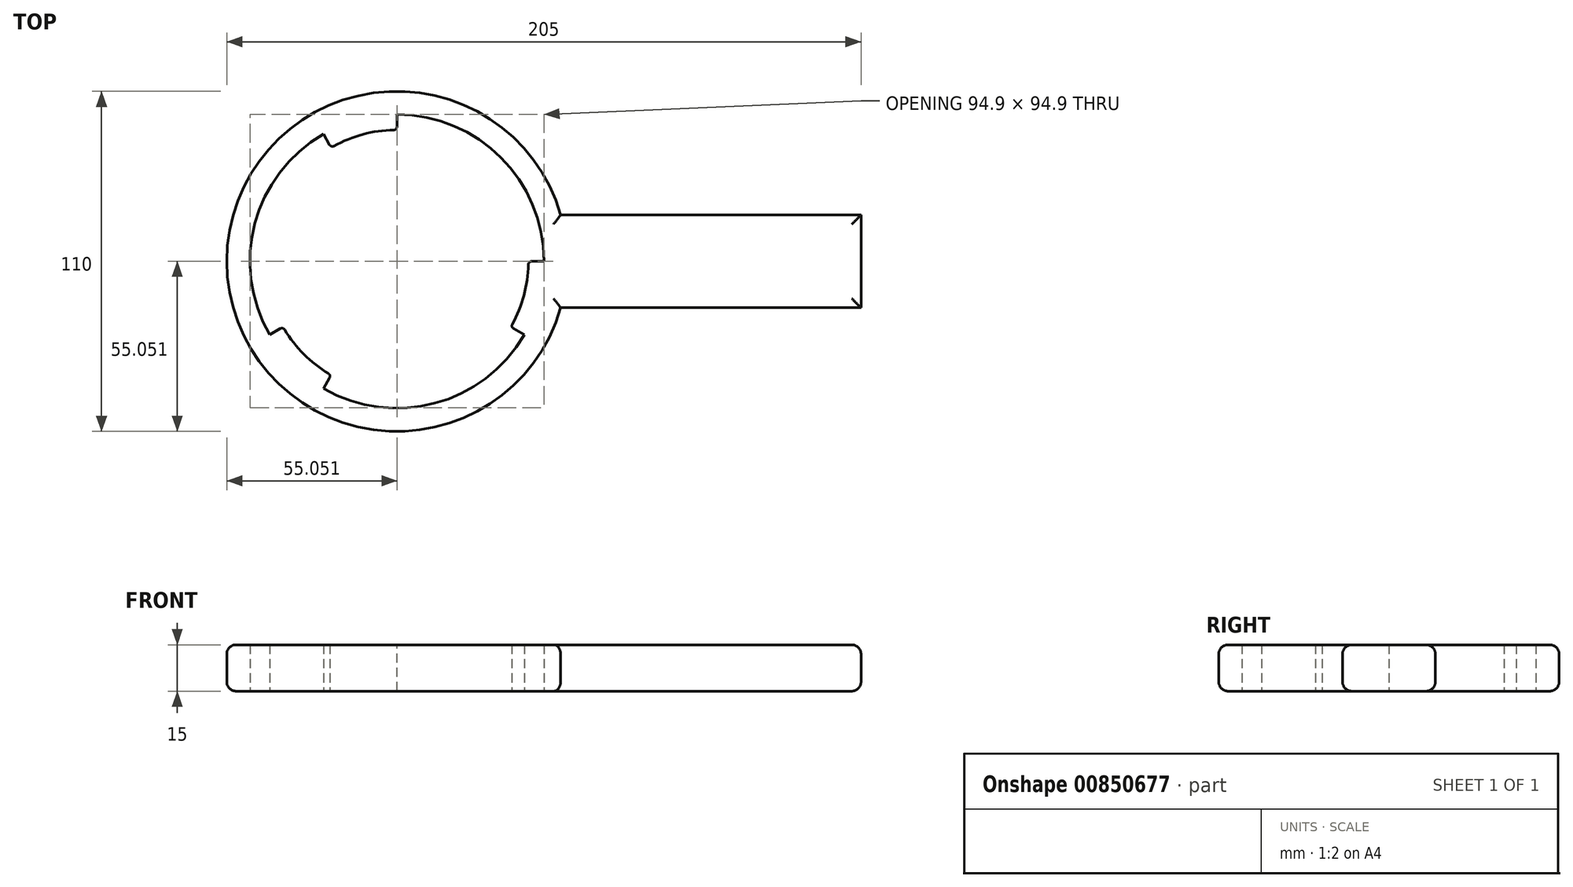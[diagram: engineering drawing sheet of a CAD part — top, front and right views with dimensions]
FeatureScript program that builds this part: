
annotation { "Feature Type Name" : "Feature", "Feature Type Description" : "" }
export const myFeature = defineFeature(function(context is Context, id is Id, definition is map)
    precondition{}
    {
        {
            var Q0;
            Q0=qCreatedBy(makeId("Top.planeOp"),FACE);
            var sketch = newSketch(context, id + "F0", { "sketchPlane" : qUnion([Q0])});
            skArc(sketch, "E0", {"start": v(-36.8, -21.25) * mm, "mid": v(-30.05, -30.05) * mm, "end": v(-21.25, -36.8) * mm});
            skArc(sketch, "E1", {"start": v(-23.75, -41.14) * mm, "mid": v(12.3, -45.88) * mm, "end": v(41.14, -23.75) * mm});
            skArc(sketch, "E2", {"start": v(52.92, 15) * mm, "mid": v(-55, 0) * mm, "end": v(52.92, -15) * mm});
            skLineSegment(sketch, "E3", {"start": v(0, 42.5) * mm, "end": v(0, 47.5) * mm});
            skLineSegment(sketch, "E4", {"start": v(-21.25, 36.8) * mm, "end": v(-23.75, 41.14) * mm});
            skLineSegment(sketch, "E5", {"start": v(-36.8, -21.25) * mm, "end": v(-41.14, -23.75) * mm});
            skLineSegment(sketch, "E6", {"start": v(-21.25, -36.8) * mm, "end": v(-23.75, -41.14) * mm});
            skLineSegment(sketch, "E7", {"start": v(36.8, -21.25) * mm, "end": v(41.14, -23.75) * mm});
            skLineSegment(sketch, "E8", {"start": v(42.5, 0) * mm, "end": v(47.5, 0) * mm});
            skArc(sketch, "E9.trimOffspring", {"start": v(0, 42.5) * mm, "mid": v(-11, 41.05) * mm, "end": v(-21.25, 36.8) * mm});
            skArc(sketch, "E10.trimOffspring", {"start": v(36.8, -21.25) * mm, "mid": v(41.05, -11) * mm, "end": v(42.5, 0) * mm});
            skArc(sketch, "E11.trimOffspring", {"start": v(-23.75, 41.14) * mm, "mid": v(-45.88, 12.3) * mm, "end": v(-41.14, -23.75) * mm});
            skArc(sketch, "E12.trimOffspring", {"start": v(47.5, 0) * mm, "mid": v(33.59, 33.59) * mm, "end": v(0, 47.5) * mm});
            skLineSegment(sketch, "E13", {"start": v(52.92, 15) * mm, "end": v(150, 15) * mm});
            skLineSegment(sketch, "E14", {"start": v(150, 15) * mm, "end": v(150, -15) * mm});
            skLineSegment(sketch, "E15", {"start": v(150, -15) * mm, "end": v(52.92, -15) * mm});
            skSolve(sketch);
        }
        {
            var Q0;
            Q0=makeQuery(id+"F0.imprint","IMPRINT",FACE,{"disambiguationData":[TD([[makeQuery(id+"F0.imprint","IMPRINT",EDGE,{"derivedFrom":sQuery(id+"F0.wireOp",EDGE,"E0")}),-1.0]])]});
            extrude(context, id + "F1", {"entities" : qUnion([Q0]), "depth" : 15 * mm, "offsetDistance" : 25 * mm});
        }
        {
            var Q0;
            Q0=makeQuery(id+"F1.opExtrude","CAP_EDGE",EDGE,{"disambiguationData":[OSD([sQuery(id+"F0.wireOp",EDGE,"E13")])],"isStart":false});
            var Q1;
            Q1=makeQuery(id+"F1.opExtrude","CAP_EDGE",EDGE,{"disambiguationData":[OSD([sQuery(id+"F0.wireOp",EDGE,"E14")])],"isStart":false});
            var Q2;
            Q2=makeQuery(id+"F1.opExtrude","CAP_EDGE",EDGE,{"disambiguationData":[OSD([sQuery(id+"F0.wireOp",EDGE,"E15")])],"isStart":false});
            var Q3;
            Q3=makeQuery(id+"F1.opExtrude","CAP_EDGE",EDGE,{"disambiguationData":[OSD([sQuery(id+"F0.wireOp",EDGE,"E2")])],"isStart":false});
            var Q4;
            Q4=makeQuery(id+"F1.opExtrude","CAP_EDGE",EDGE,{"disambiguationData":[OSD([sQuery(id+"F0.wireOp",EDGE,"E15")])],"isStart":true});
            var Q5;
            Q5=makeQuery(id+"F1.opExtrude","CAP_EDGE",EDGE,{"disambiguationData":[OSD([sQuery(id+"F0.wireOp",EDGE,"E14")])],"isStart":true});
            var Q6;
            Q6=makeQuery(id+"F1.opExtrude","CAP_EDGE",EDGE,{"disambiguationData":[OSD([sQuery(id+"F0.wireOp",EDGE,"E2")])],"isStart":true});
            var Q7;
            Q7=makeQuery(id+"F1.opExtrude","CAP_EDGE",EDGE,{"disambiguationData":[OSD([sQuery(id+"F0.wireOp",EDGE,"E13")])],"isStart":true});
            fillet(context, id + "F2", {"entities" : qUnion([Q0, Q1, Q2, Q3, Q4, Q5, Q6, Q7]), "radius" : 3 * mm, "tangentPropagation" : true, "allowEdgeOverflow" : false});
        }
        {
            var Q0;
            Q0=makeQuery(id+"F1.opExtrude","SWEPT_EDGE",EDGE,{"disambiguationData":[OSD([sQuery(id+"F0.wireOp",EDGE,"E7"),sQuery(id+"F0.wireOp",EDGE,"E10.trimOffspring")])]});
            var Q1;
            Q1=makeQuery(id+"F1.opExtrude","SWEPT_EDGE",EDGE,{"disambiguationData":[OSD([sQuery(id+"F0.wireOp",EDGE,"E8"),sQuery(id+"F0.wireOp",EDGE,"E10.trimOffspring")])]});
            var Q2;
            Q2=makeQuery(id+"F1.opExtrude","SWEPT_EDGE",EDGE,{"disambiguationData":[OSD([sQuery(id+"F0.wireOp",EDGE,"E3"),sQuery(id+"F0.wireOp",EDGE,"E9.trimOffspring")])]});
            var Q3;
            Q3=makeQuery(id+"F1.opExtrude","SWEPT_EDGE",EDGE,{"disambiguationData":[OSD([sQuery(id+"F0.wireOp",EDGE,"E4"),sQuery(id+"F0.wireOp",EDGE,"E9.trimOffspring")])]});
            var Q4;
            Q4=makeQuery(id+"F1.opExtrude","SWEPT_EDGE",EDGE,{"disambiguationData":[OSD([sQuery(id+"F0.wireOp",EDGE,"E0"),sQuery(id+"F0.wireOp",EDGE,"E6")])]});
            var Q5;
            Q5=makeQuery(id+"F1.opExtrude","SWEPT_EDGE",EDGE,{"disambiguationData":[OSD([sQuery(id+"F0.wireOp",EDGE,"E0"),sQuery(id+"F0.wireOp",EDGE,"E5")])]});
            fillet(context, id + "F3", {"entities" : qUnion([Q0, Q1, Q2, Q3, Q4, Q5]), "radius" : 1 * mm, "tangentPropagation" : true, "allowEdgeOverflow" : false});
        }
    });
